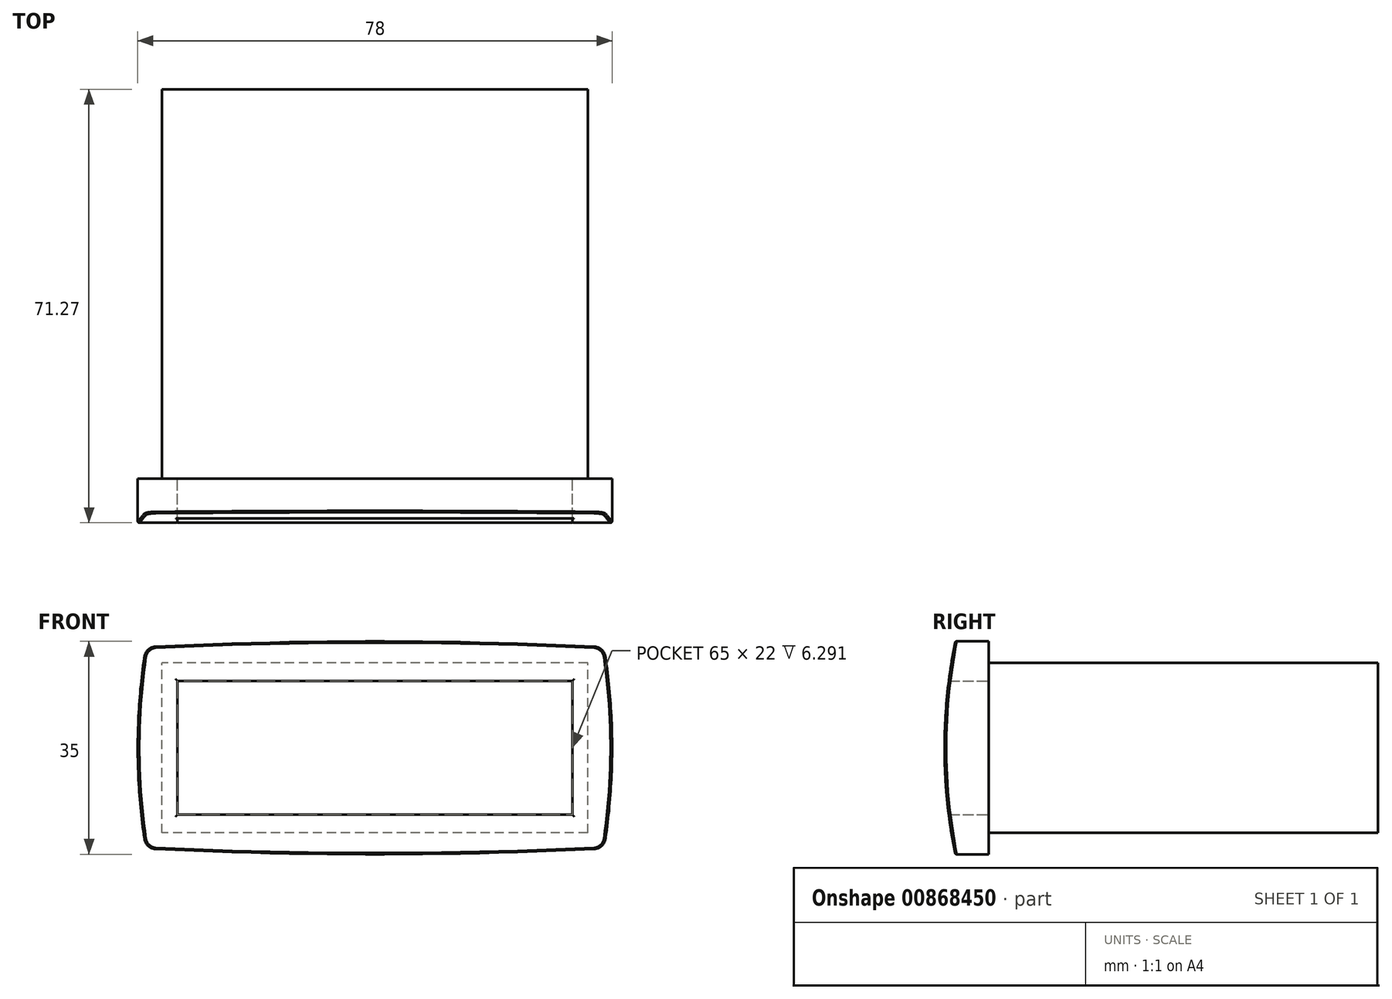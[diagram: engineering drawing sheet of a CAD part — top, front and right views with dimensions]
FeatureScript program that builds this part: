
annotation { "Feature Type Name" : "Feature", "Feature Type Description" : "" }
export const myFeature = defineFeature(function(context is Context, id is Id, definition is map)
    precondition{}
    {
        {
            var Q0;
            Q0=qCreatedBy(makeId("Front.planeOp"),FACE);
            var sketch = newSketch(context, id + "F0", { "sketchPlane" : qUnion([Q0])});
            skLineSegment(sketch, "E0.bottom", {"start": v(35, -14) * mm, "end": v(-35, -14) * mm});
            skLineSegment(sketch, "E0.top", {"start": v(35, 14) * mm, "end": v(-35, 14) * mm});
            skLineSegment(sketch, "E0.left", {"start": v(35, -14) * mm, "end": v(35, 14) * mm});
            skLineSegment(sketch, "E0.right", {"start": v(-35, -14) * mm, "end": v(-35, 14) * mm});
            skPoint(sketch, "E0.middle", {"position": v(0, 0) * mm});
            skLineSegment(sketch, "E1.bottom", {"start": v(39, -17.5) * mm, "end": v(-39, -17.5) * mm});
            skLineSegment(sketch, "E1.top", {"start": v(39, 17.5) * mm, "end": v(-39, 17.5) * mm});
            skLineSegment(sketch, "E1.left", {"start": v(39, -17.5) * mm, "end": v(39, 17.5) * mm});
            skLineSegment(sketch, "E1.right", {"start": v(-39, -17.5) * mm, "end": v(-39, 17.5) * mm});
            skLineSegment(sketch, "E2", {"start": v(-39, 16.5) * mm, "end": v(39, 16.5) * mm, "construction": true});
            skLineSegment(sketch, "E3", {"start": v(-39, -16.5) * mm, "end": v(39, -16.5) * mm, "construction": true});
            skPoint(sketch, "E4", {"position": v(0, 17.5) * mm});
            skPoint(sketch, "E5", {"position": v(0, -17.5) * mm});
            skArc(sketch, "E6", {"start": v(39, 16.5) * mm, "mid": v(0, 17.5) * mm, "end": v(-39, 16.5) * mm});
            skArc(sketch, "E7", {"start": v(-39, -16.5) * mm, "mid": v(0, -17.5) * mm, "end": v(39, -16.5) * mm});
            skLineSegment(sketch, "E8", {"start": v(-37.5, 17.5) * mm, "end": v(-37.5, -17.5) * mm, "construction": true});
            skLineSegment(sketch, "E9", {"start": v(37.5, 17.5) * mm, "end": v(37.5, -17.5) * mm, "construction": true});
            skPoint(sketch, "E10", {"position": v(-39, 0) * mm});
            skPoint(sketch, "E11", {"position": v(39, 0) * mm});
            skArc(sketch, "E12", {"start": v(-37.5, 17.5) * mm, "mid": v(-39, 0) * mm, "end": v(-37.5, -17.5) * mm});
            skArc(sketch, "E13", {"start": v(37.5, -17.5) * mm, "mid": v(39, 0) * mm, "end": v(37.5, 17.5) * mm});
            skLineSegment(sketch, "E14.bottom", {"start": v(32.5, -11) * mm, "end": v(-32.5, -11) * mm});
            skLineSegment(sketch, "E14.top", {"start": v(32.5, 11) * mm, "end": v(-32.5, 11) * mm});
            skLineSegment(sketch, "E14.left", {"start": v(32.5, -11) * mm, "end": v(32.5, 11) * mm});
            skLineSegment(sketch, "E14.right", {"start": v(-32.5, -11) * mm, "end": v(-32.5, 11) * mm});
            skSolve(sketch);
        }
        {
            var Q0;
            Q0=makeQuery(id+"F0.imprint","IMPRINT",FACE,{"disambiguationData":[TD([[makeQuery(id+"F0.imprint","IMPRINT",EDGE,{"derivedFrom":sQuery(id+"F0.wireOp",EDGE,"E14.bottom")}),-1.0]])]});
            var Q1;
            Q1=makeQuery(id+"F0.imprint","IMPRINT",FACE,{"disambiguationData":[TD([[makeQuery(id+"F0.imprint","IMPRINT",EDGE,{"derivedFrom":sQuery(id+"F0.wireOp",EDGE,"E0.bottom")}),-1.0]])]});
            extrude(context, id + "F1", {"entities" : qUnion([Q0, Q1]), "oppositeDirection" : true, "depth" : 64 * mm, "offsetDistance" : 25 * mm});
        }
        {
            var Q0;
            Q0=makeQuery(id+"F0.imprint","IMPRINT",FACE,{"disambiguationData":[TD([[makeQuery(id+"F0.imprint","IMPRINT",EDGE,{"derivedFrom":sQuery(id+"F0.wireOp",EDGE,"E0.bottom")}),1.0]])]});
            var Q1;
            Q1=makeQuery(id+"F0.imprint","IMPRINT",FACE,{"disambiguationData":[TD([[makeQuery(id+"F0.imprint","IMPRINT",EDGE,{"derivedFrom":sQuery(id+"F0.wireOp",EDGE,"E0.bottom")}),-1.0]])]});
            extrude(context, id + "F2", {"entities" : qUnion([Q0, Q1]), "operationType" : NewBodyOperationType.ADD, "depth" : 7.27 * mm, "offsetDistance" : 25 * mm});
        }
        {
            var Q0;
            Q0=makeQuery(id+"F0.imprint","IMPRINT",FACE,{"disambiguationData":[TD([[makeQuery(id+"F0.imprint","IMPRINT",EDGE,{"derivedFrom":sQuery(id+"F0.wireOp",EDGE,"E14.bottom")}),-1.0]])]});
            extrude(context, id + "F3", {"entities" : qUnion([Q0]), "depth" : 7.5 * mm, "offsetDistance" : 25 * mm});
        }
        {
            var Q0;
            Q0=qCreatedBy(makeId("Right.planeOp"),FACE);
            var sketch = newSketch(context, id + "F4", { "sketchPlane" : qUnion([Q0])});
            skLineSegment(sketch, "E15.0", {"start": v(-7.27, -16.57) * mm, "end": v(-7.27, 16.57) * mm});
            skLineSegment(sketch, "E16", {"start": v(-7.27, 17.5) * mm, "end": v(0, 17.5) * mm});
            skLineSegment(sketch, "E17", {"start": v(0, -17.5) * mm, "end": v(-7.27, -17.5) * mm});
            skLineSegment(sketch, "E18.0", {"start": v(0, -16.57) * mm, "end": v(0, 16.57) * mm});
            skLineSegment(sketch, "E19", {"start": v(-5.5, 17.5) * mm, "end": v(-5.5, -17.5) * mm});
            skPoint(sketch, "E20", {"position": v(-7.27, 0) * mm});
            skArc(sketch, "E21", {"start": v(-5.5, 17.5) * mm, "mid": v(-7.27, 0) * mm, "end": v(-5.5, -17.5) * mm});
            skLineSegment(sketch, "E22", {"start": v(-5.5, 17.5) * mm, "end": v(-11.28, 17.5) * mm});
            skLineSegment(sketch, "E23", {"start": v(-11.28, 17.5) * mm, "end": v(-11.28, -17.5) * mm});
            skLineSegment(sketch, "E24", {"start": v(-11.28, -17.5) * mm, "end": v(-5.5, -17.5) * mm});
            skSolve(sketch);
        }
        {
            var Q0;
            {var subQ0=sQuery(id+"F4.wireOp",EDGE,"E23");Q0=makeQuery(id+"F4.imprint","IMPRINT",FACE,{"disambiguationData":[TD([[makeQuery(id+"F4.imprint","IMPRINT",EDGE,{"derivedFrom":subQ0}),1.0]])]});}
            extrude(context, id + "F5", {"entities" : qUnion([Q0]), "operationType" : NewBodyOperationType.REMOVE, "oppositeDirection" : true, "depth" : 100 * mm, "offsetDistance" : 25 * mm, "symmetric" : true});
        }
        {
            var Q0;
            Q0=makeQuery(id+"F2.opExtrude","SWEPT_EDGE",EDGE,{"disambiguationData":[OSD([sQuery(id+"F0.wireOp",EDGE,"E6"),sQuery(id+"F0.wireOp",EDGE,"E12")])]});
            var Q1;
            Q1=makeQuery(id+"F2.opExtrude","SWEPT_EDGE",EDGE,{"disambiguationData":[OSD([sQuery(id+"F0.wireOp",EDGE,"E6"),sQuery(id+"F0.wireOp",EDGE,"E13")])]});
            var Q2;
            Q2=makeQuery(id+"F2.opExtrude","SWEPT_EDGE",EDGE,{"disambiguationData":[OSD([sQuery(id+"F0.wireOp",EDGE,"E7"),sQuery(id+"F0.wireOp",EDGE,"E13")])]});
            var Q3;
            Q3=makeQuery(id+"F2.opExtrude","SWEPT_EDGE",EDGE,{"disambiguationData":[OSD([sQuery(id+"F0.wireOp",EDGE,"E7"),sQuery(id+"F0.wireOp",EDGE,"E12")])]});
            fillet(context, id + "F6", {"entities" : qUnion([Q0, Q1, Q2, Q3]), "radius" : 2 * mm, "tangentPropagation" : true, "allowEdgeOverflow" : false});
        }
        {
            var Q0;
            Q0=makeQuery(id+"F5.boolean.opBoolean","COPY",FACE,{"disambiguationData":[TD([makeQuery(id+"F2.opExtrude","SWEPT_FACE",FACE,{"disambiguationData":[OSD([sQuery(id+"F0.wireOp",EDGE,"E6")])]})])],"derivedFrom":makeQuery(id+"F5.opExtrude","SWEPT_FACE",FACE,{"disambiguationData":[OSD([sQuery(id+"F4.wireOp",EDGE,"E21")])]})});
            fillet(context, id + "F7", {"entities" : qUnion([Q0]), "radius" : .25 * mm, "tangentPropagation" : true, "allowEdgeOverflow" : false});
        }
    });
